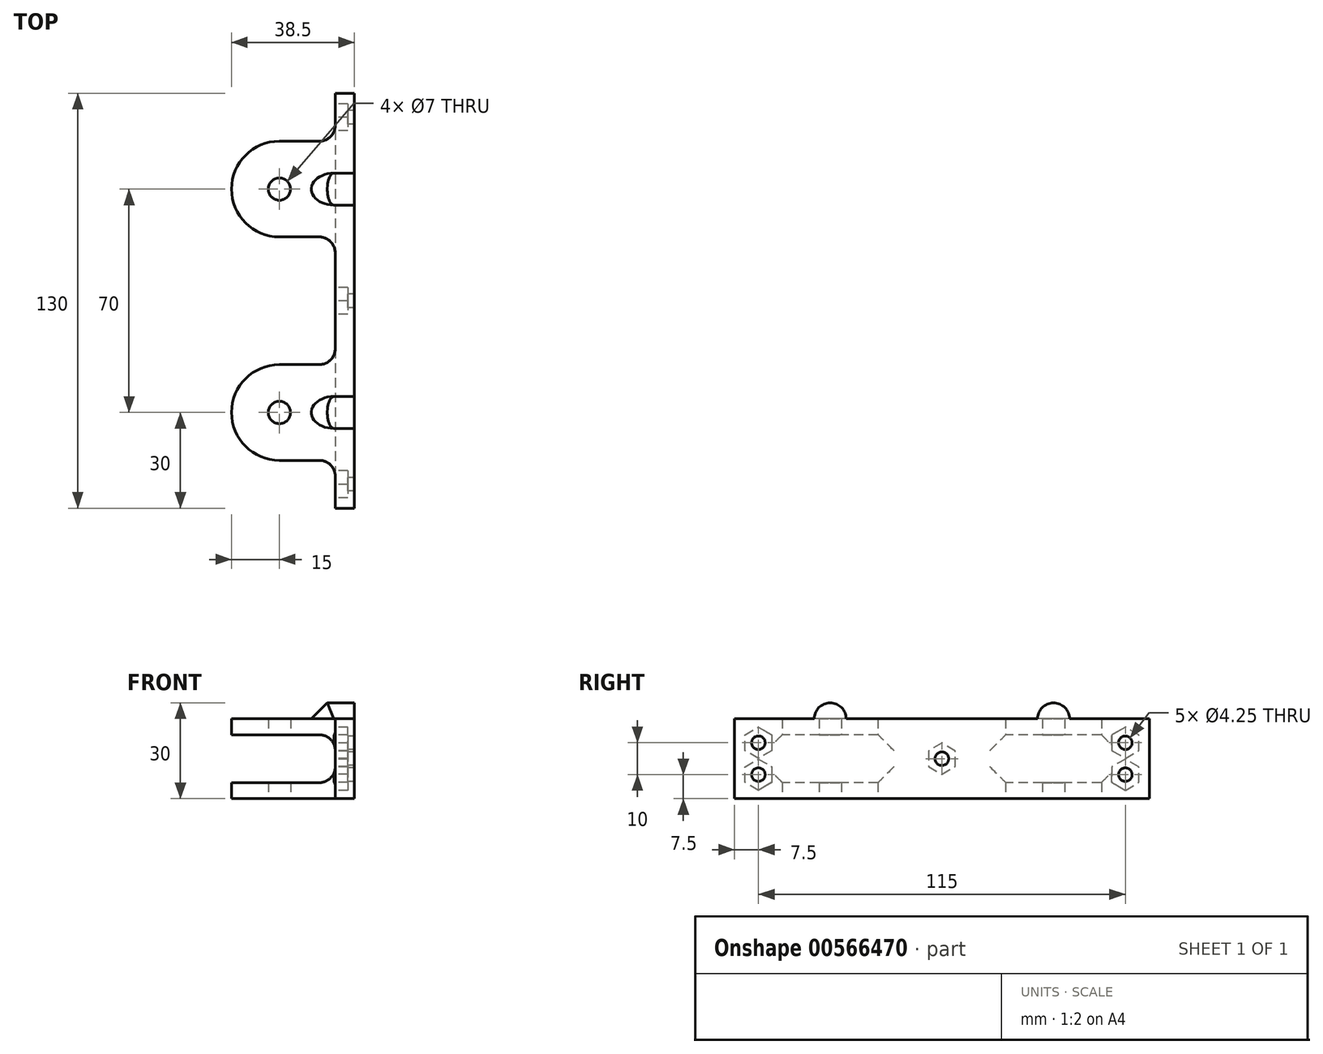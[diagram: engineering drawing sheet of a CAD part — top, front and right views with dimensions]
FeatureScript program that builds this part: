
annotation { "Feature Type Name" : "Feature", "Feature Type Description" : "" }
export const myFeature = defineFeature(function(context is Context, id is Id, definition is map)
    precondition{}
    {
        {
            var Q0;
            Q0=qCreatedBy(makeId("Top.planeOp"),FACE);
            var sketch = newSketch(context, id + "F0", { "sketchPlane" : qUnion([Q0])});
            skCircle(sketch, "E0", {"center": v(0, 35) * mm, "radius": 3.5 * mm});
            skCircle(sketch, "E1.MirrorC", {"center": v(0, -35) * mm, "radius": 3.5 * mm});
            skArc(sketch, "E2", {"start": v(0, 50) * mm, "mid": v(-15, 35) * mm, "end": v(0, 20) * mm});
            skLineSegment(sketch, "E3", {"start": v(0, 50) * mm, "end": v(17.5, 50) * mm});
            skLineSegment(sketch, "E4", {"start": v(17.5, 50) * mm, "end": v(17.5, 65) * mm});
            skLineSegment(sketch, "E5", {"start": v(17.5, 65) * mm, "end": v(23.5, 65) * mm});
            skLineSegment(sketch, "E6", {"start": v(23.5, 65) * mm, "end": v(23.5, 0) * mm});
            skLineSegment(sketch, "E7", {"start": v(0, 20) * mm, "end": v(17.5, 20) * mm});
            skLineSegment(sketch, "E8", {"start": v(17.5, 20) * mm, "end": v(17.5, 0) * mm});
            skArc(sketch, "E9.MirrorCS", {"start": v(0, -50) * mm, "mid": v(-15, -35) * mm, "end": v(0, -20) * mm});
            skLineSegment(sketch, "E10.MirrorCS", {"start": v(0, -20) * mm, "end": v(17.5, -20) * mm});
            skLineSegment(sketch, "E11.MirrorCS", {"start": v(17.5, -20) * mm, "end": v(17.5, 0) * mm});
            skLineSegment(sketch, "E12.MirrorCS", {"start": v(23.5, -65) * mm, "end": v(23.5, 0) * mm});
            skLineSegment(sketch, "E13.MirrorCS", {"start": v(0, -50) * mm, "end": v(17.5, -50) * mm});
            skLineSegment(sketch, "E14.MirrorCS", {"start": v(17.5, -50) * mm, "end": v(17.5, -65) * mm});
            skLineSegment(sketch, "E15.MirrorCS", {"start": v(17.5, -65) * mm, "end": v(23.5, -65) * mm});
            skSolve(sketch);
        }
        {
            var Q0;
            Q0=qSketchRegion(id+"F0",true);
            extrude(context, id + "F1", {"entities" : qUnion([Q0]), "endBound" : BoundingType.SYMMETRIC, "depth" : 25 * mm, "offsetDistance" : 25 * mm});
        }
        {
            var Q0;
            Q0=makeQuery(id+"F1.opExtrude","SWEPT_FACE",FACE,{"disambiguationData":[OSD([sQuery(id+"F0.wireOp",EDGE,"E4")])]});
            var sketch = newSketch(context, id + "F2", { "sketchPlane" : qUnion([Q0])});
            skCircle(sketch, "E16", {"center": v(-57.5, 5) * mm, "radius": 2.12 * mm});
            skCircle(sketch, "E17", {"center": v(-57.5, -5) * mm, "radius": 2.12 * mm});
            skLineSegment(sketch, "E18", {"start": v(-35, 25.15) * mm, "end": v(-35, 0) * mm, "construction": true});
            skCircle(sketch, "E19.MirrorC", {"center": v(57.5, 5) * mm, "radius": 2.12 * mm});
            skCircle(sketch, "E20.MirrorC", {"center": v(57.5, -5) * mm, "radius": 2.12 * mm});
            skLineSegment(sketch, "E21.MirrorCS", {"start": v(35, 25.15) * mm, "end": v(35, 0) * mm, "construction": true});
            skCircle(sketch, "E22", {"center": v(0, 0) * mm, "radius": 2.12 * mm});
            skSolve(sketch);
        }
        {
            var Q0;
            Q0=qSketchRegion(id+"F2",true);
            extrude(context, id + "F3", {"entities" : qUnion([Q0]), "operationType" : NewBodyOperationType.REMOVE, "oppositeDirection" : true, "depth" : 25 * mm});
        }
        {
            var Q0;
            Q0=makeQuery(id+"F1.opExtrude","SWEPT_FACE",FACE,{"disambiguationData":[OSD([sQuery(id+"F0.wireOp",EDGE,"E4")])]});
            var sketch = newSketch(context, id + "F4", { "sketchPlane" : qUnion([Q0])});
            skLineSegment(sketch, "E23", {"start": v(-35, 24.89) * mm, "end": v(-35, 0) * mm, "construction": true});
            skLineSegment(sketch, "E24.MirrorCS", {"start": v(35, 24.89) * mm, "end": v(35, 0) * mm, "construction": true});
            skCircle(sketch, "E25.cCircle", {"center": v(0, 0) * mm, "radius": 4.22 * mm, "construction": true});
            skLineSegment(sketch, "E25.0", {"start": v(4.22, 2.44) * mm, "end": v(4.22, -2.44) * mm});
            skLineSegment(sketch, "E25.1", {"start": v(4.23, -2.44) * mm, "end": v(0, -4.88) * mm});
            skLineSegment(sketch, "E25.2", {"start": v(0, -4.88) * mm, "end": v(-4.22, -2.44) * mm});
            skLineSegment(sketch, "E25.3", {"start": v(-4.22, -2.44) * mm, "end": v(-4.22, 2.44) * mm});
            skLineSegment(sketch, "E25.4", {"start": v(-4.22, 2.44) * mm, "end": v(0, 4.88) * mm});
            skLineSegment(sketch, "E25.5", {"start": v(0, 4.88) * mm, "end": v(4.23, 2.44) * mm});
            skPoint(sketch, "E25.0.midPoint", {"position": v(4.22, 0) * mm});
            skCircle(sketch, "E26.cCircle", {"center": v(-57.5, 5) * mm, "radius": 4.22 * mm, "construction": true});
            skLineSegment(sketch, "E26.0", {"start": v(-53.28, 7.44) * mm, "end": v(-53.28, 2.56) * mm});
            skLineSegment(sketch, "E26.1", {"start": v(-53.28, 2.56) * mm, "end": v(-57.5, 0.12) * mm});
            skLineSegment(sketch, "E26.2", {"start": v(-57.5, 0.12) * mm, "end": v(-61.73, 2.56) * mm});
            skLineSegment(sketch, "E26.3", {"start": v(-61.73, 2.56) * mm, "end": v(-61.73, 7.44) * mm});
            skLineSegment(sketch, "E26.4", {"start": v(-61.73, 7.44) * mm, "end": v(-57.5, 9.88) * mm});
            skLineSegment(sketch, "E26.5", {"start": v(-57.5, 9.88) * mm, "end": v(-53.28, 7.44) * mm});
            skPoint(sketch, "E26.0.midPoint", {"position": v(-53.28, 5) * mm});
            skCircle(sketch, "E27.cCircle", {"center": v(-57.5, -5) * mm, "radius": 4.22 * mm, "construction": true});
            skLineSegment(sketch, "E27.0", {"start": v(-53.28, -2.56) * mm, "end": v(-53.28, -7.44) * mm});
            skLineSegment(sketch, "E27.1", {"start": v(-53.28, -7.44) * mm, "end": v(-57.5, -9.88) * mm});
            skLineSegment(sketch, "E27.2", {"start": v(-57.5, -9.88) * mm, "end": v(-61.73, -7.44) * mm});
            skLineSegment(sketch, "E27.3", {"start": v(-61.73, -7.44) * mm, "end": v(-61.73, -2.56) * mm});
            skLineSegment(sketch, "E27.4", {"start": v(-61.73, -2.56) * mm, "end": v(-57.5, -0.12) * mm});
            skLineSegment(sketch, "E27.5", {"start": v(-57.5, -0.12) * mm, "end": v(-53.28, -2.56) * mm});
            skPoint(sketch, "E27.0.midPoint", {"position": v(-53.28, -5) * mm});
            skLineSegment(sketch, "E28.MirrorCS", {"start": v(61.73, 7.44) * mm, "end": v(57.5, 9.88) * mm});
            skLineSegment(sketch, "E29.MirrorCS", {"start": v(53.28, 7.44) * mm, "end": v(53.28, 2.56) * mm});
            skLineSegment(sketch, "E30.MirrorCS", {"start": v(61.73, -2.56) * mm, "end": v(57.5, -0.12) * mm});
            skLineSegment(sketch, "E31.MirrorCS", {"start": v(61.73, 2.56) * mm, "end": v(61.73, 7.44) * mm});
            skLineSegment(sketch, "E32.MirrorCS", {"start": v(57.5, 0.12) * mm, "end": v(61.72, 2.56) * mm});
            skLineSegment(sketch, "E33.MirrorCS", {"start": v(53.28, -2.56) * mm, "end": v(53.28, -7.44) * mm});
            skLineSegment(sketch, "E34.MirrorCS", {"start": v(53.28, 2.56) * mm, "end": v(57.5, 0.12) * mm});
            skLineSegment(sketch, "E35.MirrorCS", {"start": v(57.5, -9.88) * mm, "end": v(61.73, -7.44) * mm});
            skLineSegment(sketch, "E36.MirrorCS", {"start": v(61.73, -7.44) * mm, "end": v(61.73, -2.56) * mm});
            skLineSegment(sketch, "E37.MirrorCS", {"start": v(53.28, -7.44) * mm, "end": v(57.5, -9.88) * mm});
            skLineSegment(sketch, "E38.MirrorCS", {"start": v(57.5, -0.12) * mm, "end": v(53.28, -2.56) * mm});
            skLineSegment(sketch, "E39.MirrorCS", {"start": v(57.5, 9.88) * mm, "end": v(53.28, 7.44) * mm});
            skPoint(sketch, "E40.MirrorP", {"position": v(53.28, -5) * mm});
            skCircle(sketch, "E41.MirrorC", {"center": v(57.5, 5) * mm, "radius": 4.22 * mm, "construction": true});
            skPoint(sketch, "E42.MirrorP", {"position": v(53.28, 5) * mm});
            skCircle(sketch, "E43.MirrorC", {"center": v(57.5, -5) * mm, "radius": 4.22 * mm, "construction": true});
            skSolve(sketch);
        }
        {
            var Q0;
            Q0=qSketchRegion(id+"F4",true);
            extrude(context, id + "F5", {"entities" : qUnion([Q0]), "operationType" : NewBodyOperationType.REMOVE, "oppositeDirection" : true, "depth" : 4 * mm});
        }
        {
            var Q0;
            Q0=makeQuery(id+"F1.opExtrude","SWEPT_FACE",FACE,{"disambiguationData":[OSD([sQuery(id+"F0.wireOp",EDGE,"E8"),sQuery(id+"F0.wireOp",EDGE,"E11.MirrorCS")])]});
            var sketch = newSketch(context, id + "F6", { "sketchPlane" : qUnion([Q0])});
            skPoint(sketch, "E44.oppositeSnap0", {"position": v(2.09, -7.5) * mm});
            skLineSegment(sketch, "E44.bottom", {"start": v(-65, 7.5) * mm, "end": v(65, 7.5) * mm});
            skLineSegment(sketch, "E44.top", {"start": v(-65, -7.5) * mm, "end": v(65, -7.5) * mm});
            skLineSegment(sketch, "E44.left", {"start": v(-65, 7.5) * mm, "end": v(-65, -7.5) * mm});
            skLineSegment(sketch, "E44.right", {"start": v(65, 7.5) * mm, "end": v(65, -7.5) * mm});
            skSolve(sketch);
        }
        {
            var Q0;
            Q0=qSketchRegion(id+"F6",true);
            extrude(context, id + "F7", {"entities" : qUnion([Q0]), "operationType" : NewBodyOperationType.REMOVE, "endBound" : BoundingType.THROUGH_ALL, "depth" : 25 * mm});
        }
        {
            var Q0;
            {var subQ0=sQuery(id+"F6.wireOp",EDGE,"E44.bottom");Q0=makeQuery(id+"F7.boolean.opBoolean","COPY",EDGE,{"disambiguationData":[TD([makeQuery(id+"F1.opExtrude","SWEPT_FACE",FACE,{"disambiguationData":[OSD([sQuery(id+"F0.wireOp",EDGE,"E3")])]})])],"derivedFrom":makeQuery(id+"F7.opExtrude","CAP_EDGE",EDGE,{"disambiguationData":[OSD([subQ0])],"isStart":true})});}
            var Q1;
            {var subQ0=sQuery(id+"F6.wireOp",EDGE,"E44.top");Q1=makeQuery(id+"F7.boolean.opBoolean","COPY",EDGE,{"disambiguationData":[TD([makeQuery(id+"F1.opExtrude","SWEPT_FACE",FACE,{"disambiguationData":[OSD([sQuery(id+"F0.wireOp",EDGE,"E10.MirrorCS")])]})])],"derivedFrom":makeQuery(id+"F7.opExtrude","CAP_EDGE",EDGE,{"disambiguationData":[OSD([subQ0])],"isStart":true})});}
            var Q2;
            {var subQ0=sQuery(id+"F6.wireOp",EDGE,"E44.top");Q2=makeQuery(id+"F7.boolean.opBoolean","COPY",EDGE,{"disambiguationData":[TD([makeQuery(id+"F1.opExtrude","SWEPT_FACE",FACE,{"disambiguationData":[OSD([sQuery(id+"F0.wireOp",EDGE,"E3")])]})])],"derivedFrom":makeQuery(id+"F7.opExtrude","CAP_EDGE",EDGE,{"disambiguationData":[OSD([subQ0])],"isStart":true})});}
            var Q3;
            {var subQ0=sQuery(id+"F6.wireOp",EDGE,"E44.bottom");Q3=makeQuery(id+"F7.boolean.opBoolean","COPY",EDGE,{"disambiguationData":[TD([makeQuery(id+"F1.opExtrude","SWEPT_FACE",FACE,{"disambiguationData":[OSD([sQuery(id+"F0.wireOp",EDGE,"E10.MirrorCS")])]})])],"derivedFrom":makeQuery(id+"F7.opExtrude","CAP_EDGE",EDGE,{"disambiguationData":[OSD([subQ0])],"isStart":true})});}
            var Q4;
            {var subQ1=sQuery(id+"F0.wireOp",EDGE,"E8");var subQ2=sQuery(id+"F0.wireOp",EDGE,"E7");var subQ5=sQuery(id+"F6.wireOp",EDGE,"E44.bottom");Q4=makeQuery(id+"F7.boolean.opBoolean","SPLIT",EDGE,{"disambiguationData":[TD([makeQuery(id+"F7.opExtrude","SWEPT_FACE",FACE,{"disambiguationData":[OSD([subQ5])]})])],"derivedFrom":makeQuery(id+"F1.opExtrude","SWEPT_EDGE",EDGE,{"disambiguationData":[OSD([subQ2,subQ1])]})});}
            var Q5;
            {var subQ0=sQuery(id+"F0.wireOp",EDGE,"E13.MirrorCS");var subQ1=sQuery(id+"F0.wireOp",EDGE,"E14.MirrorCS");var subQ5=sQuery(id+"F6.wireOp",EDGE,"E44.bottom");Q5=makeQuery(id+"F7.boolean.opBoolean","SPLIT",EDGE,{"disambiguationData":[TD([makeQuery(id+"F7.opExtrude","SWEPT_FACE",FACE,{"disambiguationData":[OSD([subQ5])]})])],"derivedFrom":makeQuery(id+"F1.opExtrude","SWEPT_EDGE",EDGE,{"disambiguationData":[OSD([subQ0,subQ1])]})});}
            var Q6;
            {var subQ0=sQuery(id+"F0.wireOp",EDGE,"E13.MirrorCS");var subQ4=sQuery(id+"F0.wireOp",EDGE,"E14.MirrorCS");var subQ5=sQuery(id+"F6.wireOp",EDGE,"E44.top");Q6=makeQuery(id+"F7.boolean.opBoolean","SPLIT",EDGE,{"disambiguationData":[TD([makeQuery(id+"F7.opExtrude","SWEPT_FACE",FACE,{"disambiguationData":[OSD([subQ5])]})])],"derivedFrom":makeQuery(id+"F1.opExtrude","SWEPT_EDGE",EDGE,{"disambiguationData":[OSD([subQ0,subQ4])]})});}
            var Q7;
            {var subQ1=sQuery(id+"F0.wireOp",EDGE,"E8");var subQ2=sQuery(id+"F0.wireOp",EDGE,"E7");var subQ5=sQuery(id+"F6.wireOp",EDGE,"E44.top");Q7=makeQuery(id+"F7.boolean.opBoolean","SPLIT",EDGE,{"disambiguationData":[TD([makeQuery(id+"F7.opExtrude","SWEPT_FACE",FACE,{"disambiguationData":[OSD([subQ5])]})])],"derivedFrom":makeQuery(id+"F1.opExtrude","SWEPT_EDGE",EDGE,{"disambiguationData":[OSD([subQ2,subQ1])]})});}
            var Q8;
            {var subQ0=sQuery(id+"F0.wireOp",EDGE,"E10.MirrorCS");var subQ2=sQuery(id+"F0.wireOp",EDGE,"E11.MirrorCS");var subQ5=sQuery(id+"F6.wireOp",EDGE,"E44.top");Q8=makeQuery(id+"F7.boolean.opBoolean","SPLIT",EDGE,{"disambiguationData":[TD([makeQuery(id+"F7.opExtrude","SWEPT_FACE",FACE,{"disambiguationData":[OSD([subQ5])]})])],"derivedFrom":makeQuery(id+"F1.opExtrude","SWEPT_EDGE",EDGE,{"disambiguationData":[OSD([subQ0,subQ2])]})});}
            var Q9;
            {var subQ0=sQuery(id+"F0.wireOp",EDGE,"E11.MirrorCS");var subQ3=sQuery(id+"F0.wireOp",EDGE,"E10.MirrorCS");var subQ5=sQuery(id+"F6.wireOp",EDGE,"E44.bottom");Q9=makeQuery(id+"F7.boolean.opBoolean","SPLIT",EDGE,{"disambiguationData":[TD([makeQuery(id+"F7.opExtrude","SWEPT_FACE",FACE,{"disambiguationData":[OSD([subQ5])]})])],"derivedFrom":makeQuery(id+"F1.opExtrude","SWEPT_EDGE",EDGE,{"disambiguationData":[OSD([subQ3,subQ0])]})});}
            var Q10;
            {var subQ0=sQuery(id+"F0.wireOp",EDGE,"E4");var subQ3=sQuery(id+"F0.wireOp",EDGE,"E3");var subQ4=sQuery(id+"F6.wireOp",EDGE,"E44.bottom");Q10=makeQuery(id+"F7.boolean.opBoolean","SPLIT",EDGE,{"disambiguationData":[TD([makeQuery(id+"F7.opExtrude","SWEPT_FACE",FACE,{"disambiguationData":[OSD([subQ4])]})])],"derivedFrom":makeQuery(id+"F1.opExtrude","SWEPT_EDGE",EDGE,{"disambiguationData":[OSD([subQ3,subQ0])]})});}
            var Q11;
            {var subQ2=sQuery(id+"F0.wireOp",EDGE,"E3");var subQ3=sQuery(id+"F6.wireOp",EDGE,"E44.top");var subQ4=sQuery(id+"F0.wireOp",EDGE,"E4");Q11=makeQuery(id+"F7.boolean.opBoolean","SPLIT",EDGE,{"disambiguationData":[TD([makeQuery(id+"F7.opExtrude","SWEPT_FACE",FACE,{"disambiguationData":[OSD([subQ3])]})])],"derivedFrom":makeQuery(id+"F1.opExtrude","SWEPT_EDGE",EDGE,{"disambiguationData":[OSD([subQ2,subQ4])]})});}
            fillet(context, id + "F8", {"entities" : qUnion([Q0, Q1, Q2, Q3, Q4, Q5, Q6, Q7, Q8, Q9, Q10, Q11]), "radius" : 5 * mm, "tangentPropagation" : true, "allowEdgeOverflow" : false});
        }
        {
            var Q0;
            Q0=makeQuery(id+"F1.opExtrude","CAP_FACE",FACE,{"disambiguationData":[OSD([sQuery(id+"F0.wireOp",EDGE,"E0"),sQuery(id+"F0.wireOp",EDGE,"E1.MirrorC"),sQuery(id+"F0.wireOp",EDGE,"E2"),sQuery(id+"F0.wireOp",EDGE,"E3"),sQuery(id+"F0.wireOp",EDGE,"E4"),sQuery(id+"F0.wireOp",EDGE,"E5"),sQuery(id+"F0.wireOp",EDGE,"E6"),sQuery(id+"F0.wireOp",EDGE,"E7"),sQuery(id+"F0.wireOp",EDGE,"E8"),sQuery(id+"F0.wireOp",EDGE,"E9.MirrorCS"),sQuery(id+"F0.wireOp",EDGE,"E10.MirrorCS"),sQuery(id+"F0.wireOp",EDGE,"E11.MirrorCS"),sQuery(id+"F0.wireOp",EDGE,"E12.MirrorCS"),sQuery(id+"F0.wireOp",EDGE,"E13.MirrorCS"),sQuery(id+"F0.wireOp",EDGE,"E14.MirrorCS"),sQuery(id+"F0.wireOp",EDGE,"E15.MirrorCS")])],"isStart":false});
            var sketch = newSketch(context, id + "F9", { "sketchPlane" : qUnion([Q0])});
            skLineSegment(sketch, "E45.bottom", {"start": v(23.5, 40) * mm, "end": v(10, 40) * mm});
            skLineSegment(sketch, "E45.top", {"start": v(23.5, 30) * mm, "end": v(10, 30) * mm});
            skLineSegment(sketch, "E45.left", {"start": v(23.5, 40) * mm, "end": v(23.5, 30) * mm});
            skLineSegment(sketch, "E45.right", {"start": v(10, 40) * mm, "end": v(10, 30) * mm});
            skLineSegment(sketch, "E46.MirrorCS", {"start": v(23.5, -30) * mm, "end": v(10, -30) * mm});
            skLineSegment(sketch, "E47.MirrorCS", {"start": v(23.5, -40) * mm, "end": v(23.5, -30) * mm});
            skLineSegment(sketch, "E48.MirrorCS", {"start": v(23.5, -40) * mm, "end": v(10, -40) * mm});
            skLineSegment(sketch, "E49.MirrorCS", {"start": v(10, -40) * mm, "end": v(10, -30) * mm});
            skSolve(sketch);
        }
        {
            var Q0;
            Q0=qSketchRegion(id+"F9",true);
            extrude(context, id + "F10", {"entities" : qUnion([Q0]), "operationType" : NewBodyOperationType.ADD, "depth" : 5 * mm});
        }
        {
            var Q0;
            Q0=makeQuery(id+"F10.opExtrude","CAP_EDGE",EDGE,{"disambiguationData":[OSD([sQuery(id+"F9.wireOp",EDGE,"E45.right")])],"isStart":false});
            var Q1;
            Q1=makeQuery(id+"F10.opExtrude","CAP_EDGE",EDGE,{"disambiguationData":[OSD([sQuery(id+"F9.wireOp",EDGE,"E49.MirrorCS")])],"isStart":false});
            var Q2;
            Q2=makeQuery(id+"FTHjhU110Gn3oXW_1.1.F10.opExtrude","CAP_EDGE",EDGE,{"disambiguationData":[OSD([sQuery(id+"F9.wireOp",EDGE,"E45.right")])],"isStart":false});
            var Q3;
            Q3=makeQuery(id+"FTHjhU110Gn3oXW_1.1.F10.opExtrude","CAP_EDGE",EDGE,{"disambiguationData":[OSD([sQuery(id+"F9.wireOp",EDGE,"E49.MirrorCS")])],"isStart":false});
            chamfer(context, id + "F11", {"entities" : qUnion([Q0, Q1, Q2, Q3]), "width" : 5 * mm, "tangentPropagation" : true});
        }
        {
            var Q0;
            Q0=makeQuery(id+"F10.opExtrude","CAP_EDGE",EDGE,{"disambiguationData":[OSD([sQuery(id+"F9.wireOp",EDGE,"E46.MirrorCS")])],"isStart":false});
            var Q1;
            Q1=makeQuery(id+"F10.opExtrude","CAP_EDGE",EDGE,{"disambiguationData":[OSD([sQuery(id+"F9.wireOp",EDGE,"E45.bottom")])],"isStart":false});
            var Q2;
            Q2=makeQuery(id+"F10.opExtrude","CAP_EDGE",EDGE,{"disambiguationData":[OSD([sQuery(id+"F9.wireOp",EDGE,"E45.top")])],"isStart":false});
            var Q3;
            Q3=makeQuery(id+"F11.opChamfer","BLEND_EDGE",EDGE,{"blendedFrom":[makeQuery(id+"F10.opExtrude","CAP_EDGE",EDGE,{"disambiguationData":[OSD([sQuery(id+"F9.wireOp",EDGE,"E45.right")])],"isStart":false}),makeQuery(id+"F10.opExtrude","SWEPT_FACE",FACE,{"disambiguationData":[OSD([sQuery(id+"F9.wireOp",EDGE,"E45.top")])]})],"blendedInto":[makeQuery(id+"F10.opExtrude","SWEPT_FACE",FACE,{"disambiguationData":[OSD([sQuery(id+"F9.wireOp",EDGE,"E45.top")])]})]});
            var Q4;
            Q4=makeQuery(id+"F11.opChamfer","BLEND_EDGE",EDGE,{"blendedFrom":[makeQuery(id+"F10.opExtrude","CAP_EDGE",EDGE,{"disambiguationData":[OSD([sQuery(id+"F9.wireOp",EDGE,"E45.right")])],"isStart":false}),makeQuery(id+"F10.opExtrude","SWEPT_FACE",FACE,{"disambiguationData":[OSD([sQuery(id+"F9.wireOp",EDGE,"E45.bottom")])]})],"blendedInto":[makeQuery(id+"F10.opExtrude","SWEPT_FACE",FACE,{"disambiguationData":[OSD([sQuery(id+"F9.wireOp",EDGE,"E45.bottom")])]})]});
            var Q5;
            Q5=makeQuery(id+"F11.opChamfer","BLEND_EDGE",EDGE,{"blendedFrom":[makeQuery(id+"F10.opExtrude","CAP_EDGE",EDGE,{"disambiguationData":[OSD([sQuery(id+"F9.wireOp",EDGE,"E49.MirrorCS")])],"isStart":false}),makeQuery(id+"F10.opExtrude","SWEPT_FACE",FACE,{"disambiguationData":[OSD([sQuery(id+"F9.wireOp",EDGE,"E46.MirrorCS")])]})],"blendedInto":[makeQuery(id+"F10.opExtrude","SWEPT_FACE",FACE,{"disambiguationData":[OSD([sQuery(id+"F9.wireOp",EDGE,"E46.MirrorCS")])]})]});
            var Q6;
            Q6=makeQuery(id+"F11.opChamfer","BLEND_EDGE",EDGE,{"blendedFrom":[makeQuery(id+"F10.opExtrude","CAP_EDGE",EDGE,{"disambiguationData":[OSD([sQuery(id+"F9.wireOp",EDGE,"E49.MirrorCS")])],"isStart":false}),makeQuery(id+"F10.opExtrude","SWEPT_FACE",FACE,{"disambiguationData":[OSD([sQuery(id+"F9.wireOp",EDGE,"E48.MirrorCS")])]})],"blendedInto":[makeQuery(id+"F10.opExtrude","SWEPT_FACE",FACE,{"disambiguationData":[OSD([sQuery(id+"F9.wireOp",EDGE,"E48.MirrorCS")])]})]});
            var Q7;
            Q7=makeQuery(id+"F10.opExtrude","CAP_EDGE",EDGE,{"disambiguationData":[OSD([sQuery(id+"F9.wireOp",EDGE,"E48.MirrorCS")])],"isStart":false});
            var Q8;
            Q8=makeQuery(id+"F11.opChamfer","BLEND_EDGE",EDGE,{"blendedFrom":[makeQuery(id+"FTHjhU110Gn3oXW_1.1.F10.opExtrude","CAP_EDGE",EDGE,{"disambiguationData":[OSD([sQuery(id+"F9.wireOp",EDGE,"E45.right")])],"isStart":false}),makeQuery(id+"FTHjhU110Gn3oXW_1.1.F10.opExtrude","SWEPT_FACE",FACE,{"disambiguationData":[OSD([sQuery(id+"F9.wireOp",EDGE,"E45.bottom")])]})],"blendedInto":[makeQuery(id+"FTHjhU110Gn3oXW_1.1.F10.opExtrude","SWEPT_FACE",FACE,{"disambiguationData":[OSD([sQuery(id+"F9.wireOp",EDGE,"E45.bottom")])]})]});
            var Q9;
            Q9=makeQuery(id+"F11.opChamfer","BLEND_EDGE",EDGE,{"blendedFrom":[makeQuery(id+"FTHjhU110Gn3oXW_1.1.F10.opExtrude","CAP_EDGE",EDGE,{"disambiguationData":[OSD([sQuery(id+"F9.wireOp",EDGE,"E45.right")])],"isStart":false}),makeQuery(id+"FTHjhU110Gn3oXW_1.1.F10.opExtrude","SWEPT_FACE",FACE,{"disambiguationData":[OSD([sQuery(id+"F9.wireOp",EDGE,"E45.top")])]})],"blendedInto":[makeQuery(id+"FTHjhU110Gn3oXW_1.1.F10.opExtrude","SWEPT_FACE",FACE,{"disambiguationData":[OSD([sQuery(id+"F9.wireOp",EDGE,"E45.top")])]})]});
            var Q10;
            Q10=makeQuery(id+"F11.opChamfer","BLEND_EDGE",EDGE,{"blendedFrom":[makeQuery(id+"FTHjhU110Gn3oXW_1.1.F10.opExtrude","CAP_EDGE",EDGE,{"disambiguationData":[OSD([sQuery(id+"F9.wireOp",EDGE,"E49.MirrorCS")])],"isStart":false}),makeQuery(id+"FTHjhU110Gn3oXW_1.1.F10.opExtrude","SWEPT_FACE",FACE,{"disambiguationData":[OSD([sQuery(id+"F9.wireOp",EDGE,"E46.MirrorCS")])]})],"blendedInto":[makeQuery(id+"FTHjhU110Gn3oXW_1.1.F10.opExtrude","SWEPT_FACE",FACE,{"disambiguationData":[OSD([sQuery(id+"F9.wireOp",EDGE,"E46.MirrorCS")])]})]});
            var Q11;
            Q11=makeQuery(id+"F11.opChamfer","BLEND_EDGE",EDGE,{"blendedFrom":[makeQuery(id+"FTHjhU110Gn3oXW_1.1.F10.opExtrude","CAP_EDGE",EDGE,{"disambiguationData":[OSD([sQuery(id+"F9.wireOp",EDGE,"E49.MirrorCS")])],"isStart":false}),makeQuery(id+"FTHjhU110Gn3oXW_1.1.F10.opExtrude","SWEPT_FACE",FACE,{"disambiguationData":[OSD([sQuery(id+"F9.wireOp",EDGE,"E48.MirrorCS")])]})],"blendedInto":[makeQuery(id+"FTHjhU110Gn3oXW_1.1.F10.opExtrude","SWEPT_FACE",FACE,{"disambiguationData":[OSD([sQuery(id+"F9.wireOp",EDGE,"E48.MirrorCS")])]})]});
            fillet(context, id + "F12", {"entities" : qUnion([Q0, Q1, Q2, Q3, Q4, Q5, Q6, Q7, Q8, Q9, Q10, Q11]), "radius" : 5 * mm, "tangentPropagation" : true, "allowEdgeOverflow" : false});
        }
    });
